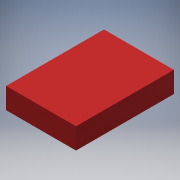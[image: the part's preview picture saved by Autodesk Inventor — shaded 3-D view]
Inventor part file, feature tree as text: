
AUTODESK INVENTOR PART (.ipt)
format: ipt  version: 2017 SP1 (Build 210196100, 196)  size: 91,136 bytes
history: native  units: in
note: dims shown in document units (in); Inventor stores cm internally (conversion verified against a paired STEP export)
features: extrude x1, sketch x1
ambient origin geometry x8: Origin, YZ Plane, XZ Plane, XY Plane, X Axis, Y Axis, Z Axis, Center Point
bodies: Solid1 (feature_tree)
feature tree (2):
  extrude  "Extrusion1"  Depth=3.5in
  sketch  "Sketch1"  dims[d0=2.5in d1=3.5in d2=0.75in d3=0.0in]
